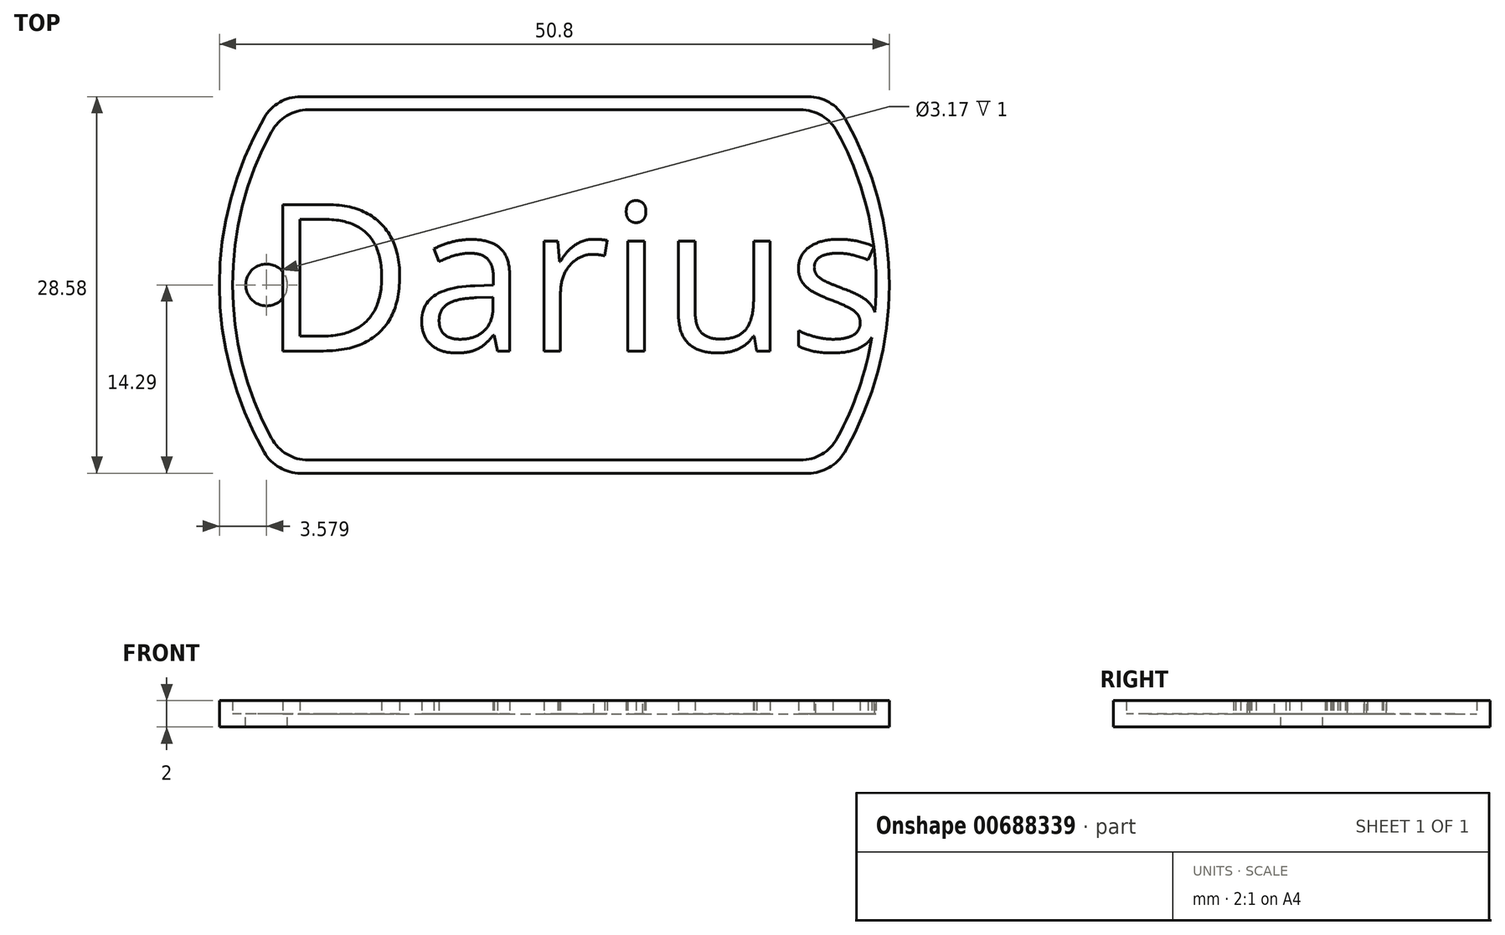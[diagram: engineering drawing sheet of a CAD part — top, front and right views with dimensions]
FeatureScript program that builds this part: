
annotation { "Feature Type Name" : "Feature", "Feature Type Description" : "" }
export const myFeature = defineFeature(function(context is Context, id is Id, definition is map)
    precondition{}
    {
        {
            var Q0;
            Q0=qCreatedBy(makeId("Top.planeOp"),FACE);
            var sketch = newSketch(context, id + "F0", { "sketchPlane" : qUnion([Q0])});
            skArc(sketch, "E0", {"start": v(-22, 12.7) * mm, "mid": v(-25.4, 0) * mm, "end": v(-22, -12.7) * mm});
            skLineSegment(sketch, "E1.top", {"start": v(-19.25, -14.29) * mm, "end": v(19.25, -14.29) * mm});
            skArc(sketch, "E2.trimOffspring", {"start": v(22, -12.7) * mm, "mid": v(25.4, 0) * mm, "end": v(22, 12.7) * mm});
            skLineSegment(sketch, "E3", {"start": v(-19.25, 14.29) * mm, "end": v(19.25, 14.29) * mm});
            skPoint(sketch, "E4.visualSharp", {"position": v(-21, 14.29) * mm});
            skArc(sketch, "E4.filletArc", {"start": v(-19.25, 14.29) * mm, "mid": v(-20.83, 13.86) * mm, "end": v(-22, 12.7) * mm});
            skPoint(sketch, "E5.visualSharp", {"position": v(21, 14.29) * mm});
            skArc(sketch, "E5.filletArc", {"start": v(22, 12.7) * mm, "mid": v(20.83, 13.86) * mm, "end": v(19.25, 14.29) * mm});
            skPoint(sketch, "E6.visualSharp", {"position": v(21, -14.29) * mm});
            skArc(sketch, "E6.filletArc", {"start": v(19.25, -14.29) * mm, "mid": v(20.83, -13.86) * mm, "end": v(22, -12.7) * mm});
            skPoint(sketch, "E7.visualSharp", {"position": v(-21, -14.29) * mm});
            skArc(sketch, "E7.filletArc", {"start": v(-22, -12.7) * mm, "mid": v(-20.83, -13.86) * mm, "end": v(-19.25, -14.29) * mm});
            skSolve(sketch);
        }
        {
            var Q0;
            Q0=makeQuery(id+"F0.imprint","IMPRINT",FACE,{"disambiguationData":[TD([[makeQuery(id+"F0.imprint","IMPRINT",EDGE,{"derivedFrom":sQuery(id+"F0.wireOp",EDGE,"E0")}),1.0]])]});
            extrude(context, id + "F1", {"entities" : qUnion([Q0]), "depth" : 1 * mm, "offsetDistance" : 25.4 * mm});
        }
        {
            var Q0;
            Q0=makeQuery(id+"F1.opExtrude","CAP_FACE",FACE,{"disambiguationData":[OSD([sQuery(id+"F0.wireOp",EDGE,"E0"),sQuery(id+"F0.wireOp",EDGE,"E1.top"),sQuery(id+"F0.wireOp",EDGE,"E2.trimOffspring"),sQuery(id+"F0.wireOp",EDGE,"E3"),sQuery(id+"F0.wireOp",EDGE,"E4.filletArc"),sQuery(id+"F0.wireOp",EDGE,"E5.filletArc"),sQuery(id+"F0.wireOp",EDGE,"E6.filletArc"),sQuery(id+"F0.wireOp",EDGE,"E7.filletArc")])],"isStart":false});
            var sketch = newSketch(context, id + "F2", { "sketchPlane" : qUnion([Q0])});
            skLineSegment(sketch, "E8.0", {"start": v(-18.66, 13.29) * mm, "end": v(18.66, 13.29) * mm});
            skArc(sketch, "E8.1", {"start": v(-21.45, 11.63) * mm, "mid": v(-24.4, 0) * mm, "end": v(-21.45, -11.63) * mm});
            skLineSegment(sketch, "E8.2", {"start": v(-18.66, -13.29) * mm, "end": v(18.66, -13.29) * mm});
            skArc(sketch, "E8.3", {"start": v(21.45, -11.63) * mm, "mid": v(24.4, 0) * mm, "end": v(21.45, 11.63) * mm});
            skPoint(sketch, "E9.visualSharp", {"position": v(-20.46, 13.29) * mm});
            skArc(sketch, "E9.filletArc", {"start": v(-18.66, 13.29) * mm, "mid": v(-20.29, 12.84) * mm, "end": v(-21.45, 11.63) * mm});
            skPoint(sketch, "E10.visualSharp", {"position": v(20.46, 13.29) * mm});
            skArc(sketch, "E10.filletArc", {"start": v(21.45, 11.63) * mm, "mid": v(20.29, 12.84) * mm, "end": v(18.66, 13.29) * mm});
            skPoint(sketch, "E11.visualSharp", {"position": v(20.46, -13.29) * mm});
            skArc(sketch, "E11.filletArc", {"start": v(18.66, -13.29) * mm, "mid": v(20.29, -12.84) * mm, "end": v(21.45, -11.63) * mm});
            skPoint(sketch, "E12.visualSharp", {"position": v(-20.46, -13.29) * mm});
            skArc(sketch, "E12.filletArc", {"start": v(-21.45, -11.63) * mm, "mid": v(-20.29, -12.84) * mm, "end": v(-18.66, -13.29) * mm});
            skLineSegment(sketch, "E13.0", {"start": v(-19.25, 14.29) * mm, "end": v(19.25, 14.29) * mm});
            skArc(sketch, "E13.1", {"start": v(-22, 12.7) * mm, "mid": v(-25.4, 0) * mm, "end": v(-22, -12.7) * mm});
            skLineSegment(sketch, "E13.2", {"start": v(-19.25, -14.29) * mm, "end": v(19.25, -14.29) * mm});
            skArc(sketch, "E13.3", {"start": v(22, -12.7) * mm, "mid": v(25.4, 0) * mm, "end": v(22, 12.7) * mm});
            skPoint(sketch, "E14.visualSharp", {"position": v(-21, -14.29) * mm});
            skArc(sketch, "E14.filletArc", {"start": v(-22, -12.7) * mm, "mid": v(-20.83, -13.86) * mm, "end": v(-19.25, -14.29) * mm});
            skPoint(sketch, "E15.visualSharp", {"position": v(21, -14.29) * mm});
            skArc(sketch, "E15.filletArc", {"start": v(19.25, -14.29) * mm, "mid": v(20.83, -13.86) * mm, "end": v(22, -12.7) * mm});
            skPoint(sketch, "E16.visualSharp", {"position": v(21, 14.29) * mm});
            skArc(sketch, "E16.filletArc", {"start": v(22, 12.7) * mm, "mid": v(20.83, 13.86) * mm, "end": v(19.25, 14.29) * mm});
            skPoint(sketch, "E17.visualSharp", {"position": v(-21, 14.29) * mm});
            skArc(sketch, "E17.filletArc", {"start": v(-19.25, 14.29) * mm, "mid": v(-20.83, 13.86) * mm, "end": v(-22, 12.7) * mm});
            skSolve(sketch);
        }
        {
            var Q0;
            Q0=makeQuery(id+"F2.imprint","IMPRINT",FACE,{"disambiguationData":[TD([[makeQuery(id+"F2.imprint","IMPRINT",EDGE,{"derivedFrom":sQuery(id+"F2.wireOp",EDGE,"E8.0")}),1.0]])]});
            extrude(context, id + "F3", {"entities" : qUnion([Q0]), "operationType" : NewBodyOperationType.ADD, "depth" : 1 * mm, "offsetDistance" : 25.4 * mm});
        }
        {
            var Q0;
            Q0=makeQuery(id+"F1.opExtrude","CAP_FACE",FACE,{"disambiguationData":[OSD([sQuery(id+"F0.wireOp",EDGE,"E0"),sQuery(id+"F0.wireOp",EDGE,"E1.top"),sQuery(id+"F0.wireOp",EDGE,"E2.trimOffspring"),sQuery(id+"F0.wireOp",EDGE,"E3"),sQuery(id+"F0.wireOp",EDGE,"E4.filletArc"),sQuery(id+"F0.wireOp",EDGE,"E5.filletArc"),sQuery(id+"F0.wireOp",EDGE,"E6.filletArc"),sQuery(id+"F0.wireOp",EDGE,"E7.filletArc")])],"isStart":false});
            var sketch = newSketch(context, id + "F4", { "sketchPlane" : qUnion([Q0])});
            skCircle(sketch, "E18", {"center": v(-21.82, 0) * mm, "radius": 1.59 * mm});
            skSolve(sketch);
        }
        {
            var Q0;
            Q0=makeQuery(id+"F4.imprint","IMPRINT",FACE,{"disambiguationData":[TD([[makeQuery(id+"F4.imprint","IMPRINT",EDGE,{"derivedFrom":sQuery(id+"F4.wireOp",EDGE,"E18")}),1.0]])]});
            extrude(context, id + "F5", {"entities" : qUnion([Q0]), "operationType" : NewBodyOperationType.REMOVE, "oppositeDirection" : true, "depth" : 1 * mm, "offsetDistance" : 25.4 * mm});
        }
        {
            var Q0;
            Q0=makeQuery(id+"F2.imprint","IMPRINT",FACE,{"disambiguationData":[TD([[makeQuery(id+"F2.imprint","IMPRINT",EDGE,{"derivedFrom":sQuery(id+"F2.wireOp",EDGE,"E8.0")}),-1.0]])]});
            var sketch = newSketch(context, id + "F6", { "sketchPlane" : qUnion([Q0])});
            skText(sketch, "E19", { "text": "Darius", "fontName": "OpenSans-Regular.ttf"});
            const initialGuessF6  = {"E19": [-0.02212, -0.00501, 1, 0, 0.0112]};
            skSetInitialGuess(sketch, initialGuessF6);
            skSolve(sketch);
        }
        {
            var Q0;
            Q0 = qSketchRegion(id + "F6", true);
            extrude(context, id + "F7", {"entities" : qUnion([Q0]), "operationType" : NewBodyOperationType.ADD, "depth" : 1 * mm, "offsetDistance" : 25.4 * mm});
        }
    });
